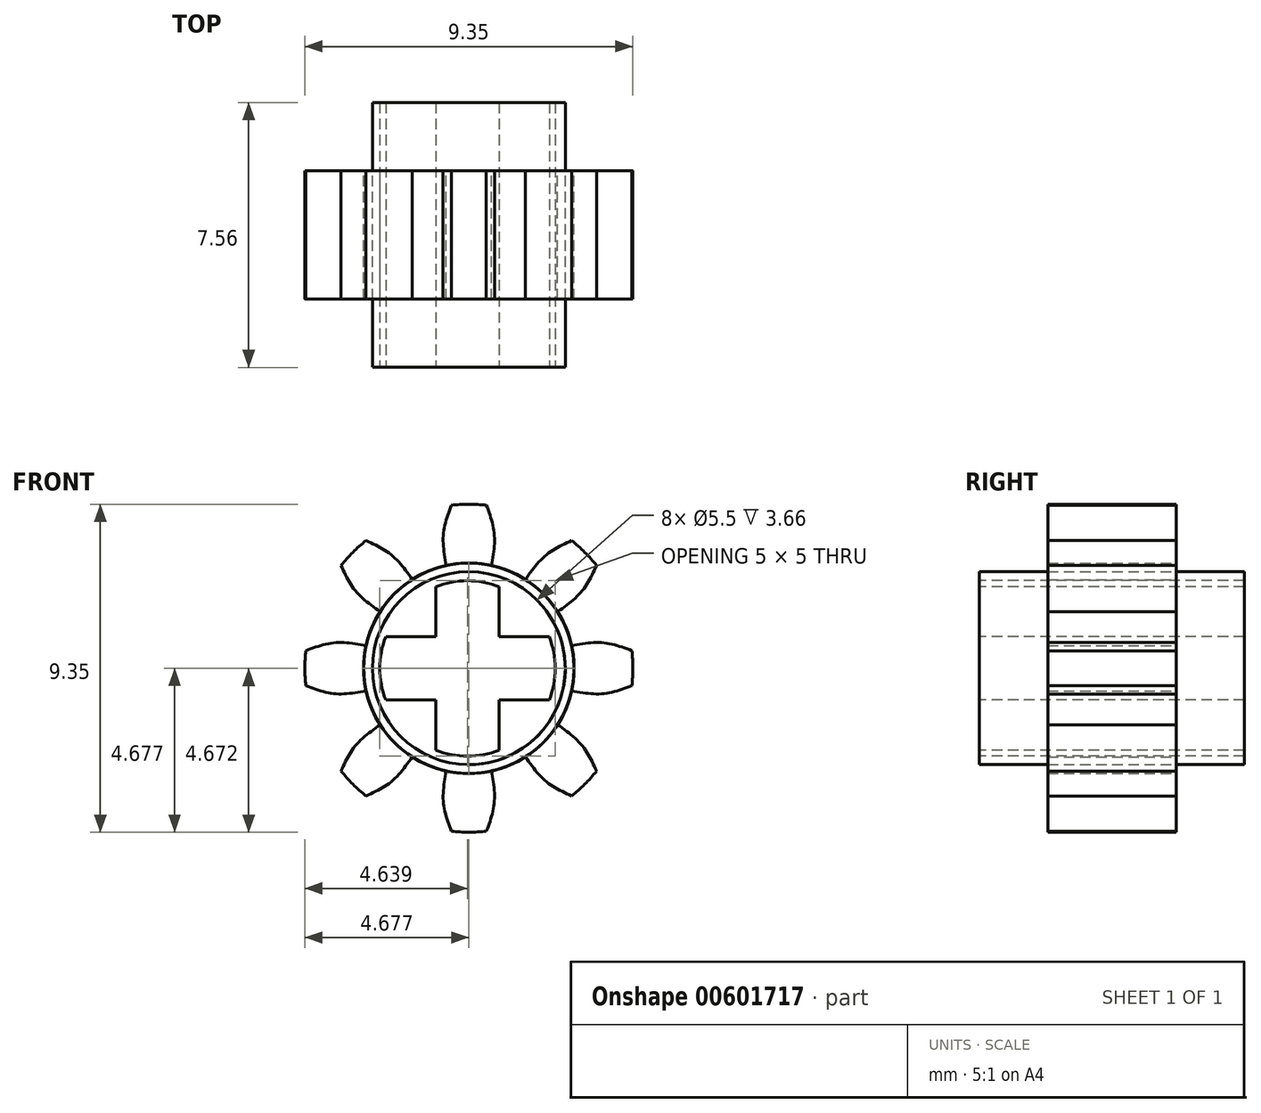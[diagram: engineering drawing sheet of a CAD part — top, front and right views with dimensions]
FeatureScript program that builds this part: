
annotation { "Feature Type Name" : "Feature", "Feature Type Description" : "" }
export const myFeature = defineFeature(function(context is Context, id is Id, definition is map)
    precondition{}
    {
        {
            var Q0;
            Q0=qCreatedBy(makeId("Front.planeOp"),FACE);
            var sketch = newSketch(context, id + "F0", { "sketchPlane" : qUnion([Q0])});
            skCircle(sketch, "E0", {"center": v(0, -2.86) * mm, "radius": 4.68 * mm});
            skCircle(sketch, "E1", {"center": v(0, -2.86) * mm, "radius": 3 * mm});
            skLineSegment(sketch, "E2", {"start": v(-0.72, 0.05) * mm, "end": v(0, 0.05) * mm, "construction": true});
            skLineSegment(sketch, "E3", {"start": v(0, 0.05) * mm, "end": v(0.73, 0.05) * mm, "construction": true});
            skLineSegment(sketch, "E4", {"start": v(-0.64, 0.07) * mm, "end": v(0, 0.07) * mm, "construction": true});
            skLineSegment(sketch, "E5", {"start": v(0, 0.07) * mm, "end": v(0.66, 0.07) * mm, "construction": true});
            skLineSegment(sketch, "E6", {"start": v(-0.5, 1.79) * mm, "end": v(0, 1.79) * mm, "construction": true});
            skLineSegment(sketch, "E7", {"start": v(0, 1.79) * mm, "end": v(0.5, 1.79) * mm, "construction": true});
            skLineSegment(sketch, "E8", {"start": v(0, 0.14) * mm, "end": v(0, 1.81) * mm, "construction": true});
            skLineSegment(sketch, "E9", {"start": v(0.86, 0.97) * mm, "end": v(-1.06, 0.97) * mm, "construction": true});
            skPoint(sketch, "E9.startSnap0", {"position": v(0, 0.97) * mm});
            skFitSpline(sketch, "E10", {"points": [v(-0.5, 1.79) * mm, v(-0.72, 0.97) * mm, v(-0.64, 0.07) * mm], "startDerivative": vector(-0.6, -1.62) * mm, "endDerivative": vector(0.3, -1.81) * mm});
            skFitSpline(sketch, "E11", {"points": [v(0.5, 1.79) * mm, v(0.73, 0.97) * mm, v(0.66, 0.07) * mm], "startDerivative": vector(0.6, -1.62) * mm, "endDerivative": vector(-0.3, -1.81) * mm});
            skCircle(sketch, "E12", {"center": v(0, -2.86) * mm, "radius": 2.75 * mm});
            skSolve(sketch);
        }
        {
            var Q0;
            {var subQ0=sQuery(id+"F0.wireOp",EDGE,"E10");Q0=makeQuery(id+"F0.imprint","IMPRINT",FACE,{"disambiguationData":[TD([[makeQuery(id+"F0.imprint","IMPRINT",EDGE,{"derivedFrom":subQ0}),1.0]])]});}
            var Q1;
            Q1=makeQuery(id+"F0.imprint","IMPRINT",FACE,{"disambiguationData":[TD([[makeQuery(id+"F0.imprint","IMPRINT",EDGE,{"derivedFrom":sQuery(id+"F0.wireOp",EDGE,"E12")}),-1.0]])]});
            extrude(context, id + "F1", {"entities" : qUnion([Q0, Q1]), "endBound" : BoundingType.SYMMETRIC, "depth" : 3.66 * mm, "offsetDistance" : 25 * mm});
        }
        {
            var Q0;
            Q0=makeQuery(id+"F1.opExtrude","SWEPT_BODY",BODY,{"disambiguationData":[OSD([sQuery(id+"F0.wireOp",EDGE,"E0"),sQuery(id+"F0.wireOp",EDGE,"E1"),sQuery(id+"F0.wireOp",EDGE,"E10"),sQuery(id+"F0.wireOp",EDGE,"E11"),sQuery(id+"F0.wireOp",EDGE,"E12")])]});
            var Q1;
            Q1=makeQuery(id+"F1.opExtrude","SWEPT_FACE",FACE,{"disambiguationData":[OSD([sQuery(id+"F0.wireOp",EDGE,"E1")])]});
            circularPattern(context, id + "F2", {"entities" : qUnion([Q0]), "axis" : qUnion([Q1]), "angle" : 360 * degree, "instanceCount" : 8, "equalSpace" : true});
        }
        {
            var Q0;
            Q0=makeQuery(id+"F0.imprint","IMPRINT",FACE,{"disambiguationData":[TD([[makeQuery(id+"F0.imprint","IMPRINT",EDGE,{"derivedFrom":sQuery(id+"F0.wireOp",EDGE,"E12")}),1.0]])]});
            extrude(context, id + "F3", {"entities" : qUnion([Q0]), "endBound" : BoundingType.SYMMETRIC, "depth" : 7.55 * mm, "offsetDistance" : 25 * mm});
        }
        {
            var Q0;
            Q0=makeQuery(id+"F3.opExtrude","CAP_FACE",FACE,{"disambiguationData":[OSD([sQuery(id+"F0.wireOp",EDGE,"E12")])],"isStart":false});
            var sketch = newSketch(context, id + "F4", { "sketchPlane" : qUnion([Q0])});
            skCircle(sketch, "E13", {"center": v(-0.03, -2.87) * mm, "radius": 2.5 * mm});
            skLineSegment(sketch, "E14", {"start": v(0.87, -3.77) * mm, "end": v(0.87, -5.2) * mm});
            skLineSegment(sketch, "E15", {"start": v(0.87, -1.97) * mm, "end": v(0.87, -0.54) * mm});
            skLineSegment(sketch, "E16", {"start": v(0.87, -1.97) * mm, "end": v(2.3, -1.97) * mm});
            skLineSegment(sketch, "E17", {"start": v(0.87, -3.77) * mm, "end": v(2.3, -3.77) * mm});
            skLineSegment(sketch, "E18", {"start": v(-0.93, -3.77) * mm, "end": v(-0.93, -5.2) * mm});
            skLineSegment(sketch, "E19", {"start": v(-0.93, -1.97) * mm, "end": v(-0.93, -0.54) * mm});
            skLineSegment(sketch, "E20", {"start": v(-0.93, -1.97) * mm, "end": v(-2.36, -1.97) * mm});
            skLineSegment(sketch, "E21", {"start": v(-0.93, -3.77) * mm, "end": v(-2.36, -3.77) * mm});
            skLineSegment(sketch, "E22", {"start": v(-0.03, -1.6) * mm, "end": v(-0.03, -4) * mm, "construction": true});
            skLineSegment(sketch, "E23", {"start": v(-1.33, -2.87) * mm, "end": v(1.24, -2.87) * mm, "construction": true});
            skSolve(sketch);
        }
        {
            var Q0;
            {var subQ4=sQuery(id+"F4.wireOp",EDGE,"E14");Q0=makeQuery(id+"F4.imprint","IMPRINT",FACE,{"disambiguationData":[TD([[makeQuery(id+"F4.imprint","IMPRINT",EDGE,{"derivedFrom":subQ4}),-1.0]])]});}
            extrude(context, id + "F5", {"entities" : qUnion([Q0]), "operationType" : NewBodyOperationType.REMOVE, "endBound" : BoundingType.THROUGH_ALL, "oppositeDirection" : true, "depth" : 7.55 * mm, "offsetDistance" : 25 * mm});
        }
    });
